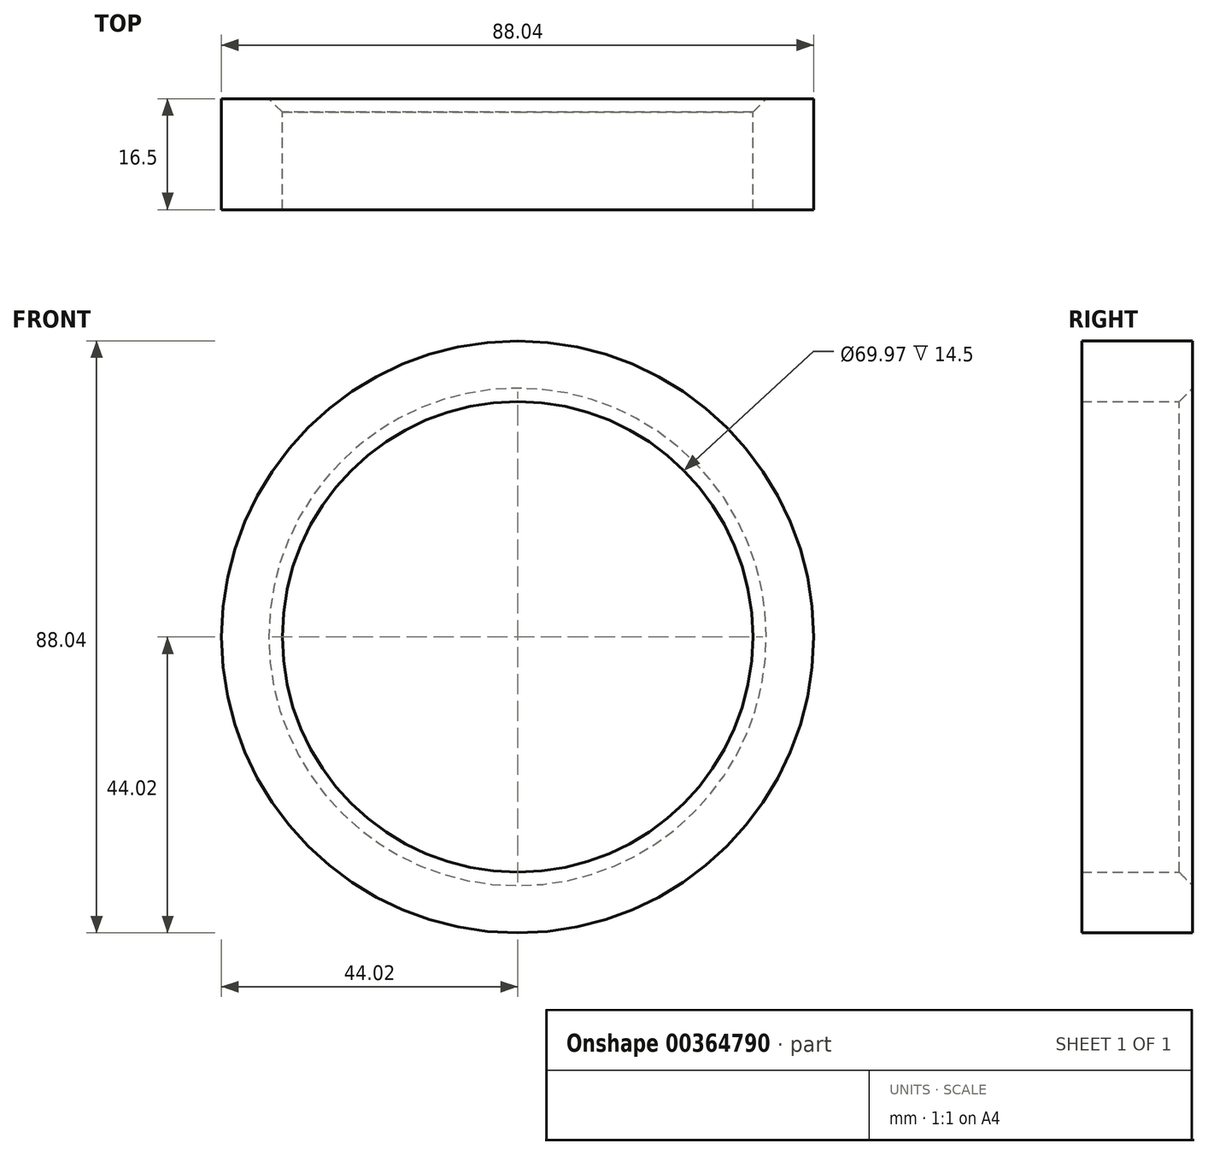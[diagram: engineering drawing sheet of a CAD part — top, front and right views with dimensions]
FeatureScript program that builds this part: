
annotation { "Feature Type Name" : "Feature", "Feature Type Description" : "" }
export const myFeature = defineFeature(function(context is Context, id is Id, definition is map)
    precondition{}
    {
        {
            var Q0;
            Q0=qCreatedBy(makeId("Front.planeOp"),FACE);
            var sketch = newSketch(context, id + "F0", { "sketchPlane" : qUnion([Q0])});
            skCircle(sketch, "E0", {"center": v(0, 0) * mm, "radius": 44.02 * mm});
            skCircle(sketch, "E1", {"center": v(0, 0) * mm, "radius": 34.98 * mm});
            skSolve(sketch);
        }
        {
            var Q0;
            Q0=makeQuery(id+"F0.imprint","IMPRINT",FACE,{"disambiguationData":[TD([[makeQuery(id+"F0.imprint","IMPRINT",EDGE,{"derivedFrom":sQuery(id+"F0.wireOp",EDGE,"E0")}),1.0]])]});
            extrude(context, id + "F1", {"entities" : qUnion([Q0]), "depth" : 16.5 * mm});
        }
        {
            var Q0;
            Q0=makeQuery(id+"F1.opExtrude","CAP_EDGE",EDGE,{"disambiguationData":[OSD([sQuery(id+"F0.wireOp",EDGE,"E1")])],"isStart":true});
            chamfer(context, id + "F2", {"entities" : qUnion([Q0]), "width" : 2 * mm, "tangentPropagation" : true});
        }
    });
